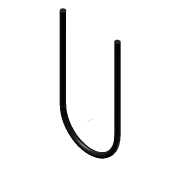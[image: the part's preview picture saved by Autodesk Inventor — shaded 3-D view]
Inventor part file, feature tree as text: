
AUTODESK INVENTOR PART (.ipt)
format: ipt  version: unknown  size: 180,224 bytes
history: native  units: in
note: dims shown in document units (in); Inventor stores cm internally (conversion verified against a paired STEP export)
features: sketch x2, sweep x1, other x1
ambient origin geometry x8: Origin, YZ Plane, XZ Plane, XY Plane, X Axis, Y Axis, Z Axis, Center Point
feature tree (4):
  sweep  "Sweep5"
  other  "Work Axis9"
  sketch  "Sketch10"  dims[d24=0.0in d33=0.7087in]
  sketch  "Sketch15"  dims[d35=0.0in d45=0.2362in d46=0.0394in d47=0.0in d56=0.2362in]
